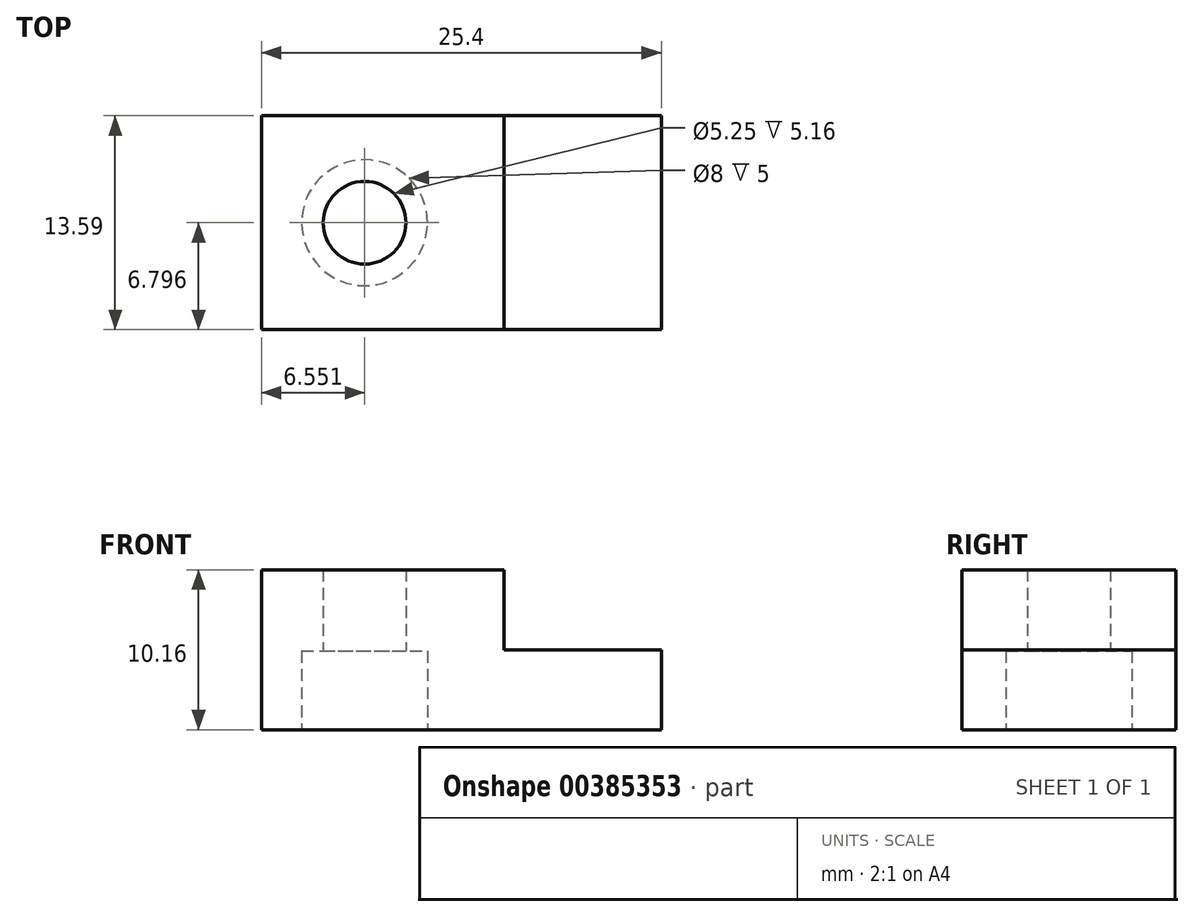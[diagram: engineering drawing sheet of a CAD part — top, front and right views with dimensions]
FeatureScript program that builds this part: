
annotation { "Feature Type Name" : "Feature", "Feature Type Description" : "" }
export const myFeature = defineFeature(function(context is Context, id is Id, definition is map)
    precondition{}
    {
        {
            var Q0;
            Q0=qCreatedBy(makeId("Top.planeOp"),FACE);
            var sketch = newSketch(context, id + "F0", { "sketchPlane" : qUnion([Q0])});
            skLineSegment(sketch, "E0.bottom", {"start": v(0, 0) * mm, "end": v(25.4, 0) * mm});
            skLineSegment(sketch, "E0.top", {"start": v(0, 13.6) * mm, "end": v(25.4, 13.6) * mm});
            skLineSegment(sketch, "E0.left", {"start": v(0, 0) * mm, "end": v(0, 13.6) * mm});
            skLineSegment(sketch, "E0.right", {"start": v(25.4, 0) * mm, "end": v(25.4, 13.6) * mm});
            skPoint(sketch, "E1", {"position": v(6.55, 6.8) * mm});
            skPoint(sketch, "E1.positionSnap0", {"position": v(0, 6.8) * mm});
            skSolve(sketch);
        }
        {
            var Q0;
            Q0=makeQuery(id+"F0.imprint","IMPRINT",FACE,{"disambiguationData":[TD([[makeQuery(id+"F0.imprint","IMPRINT",EDGE,{"derivedFrom":sQuery(id+"F0.wireOp",EDGE,"E0.bottom")}),1.0]])]});
            extrude(context, id + "F1", {"entities" : qUnion([Q0]), "depth" : 10.16 * mm});
        }
        {
            var Q0;
            Q0=sQuery(id+"F0.wireOp",VERTEX,"E1");
            var Q1;
            Q1=makeQuery(id+"F1.opExtrude","SWEPT_BODY",BODY,{"disambiguationData":[OSD([sQuery(id+"F0.wireOp",EDGE,"E0.bottom"),sQuery(id+"F0.wireOp",EDGE,"E0.top"),sQuery(id+"F0.wireOp",EDGE,"E0.left"),sQuery(id+"F0.wireOp",EDGE,"E0.right")])]});
            hole(context, id + "F2", {"style" : HoleStyle.C_BORE, "endStyle" : HoleEndStyle.THROUGH, "oppositeDirection" : true, "holeDiameter" : 5.25 * mm, "cBoreDiameter" : 8 * mm, "cBoreDepth" : 5 * mm, "isTappedThrough" : true, "tappedDepth" : 12.7 * mm, "tapClearance" : 3, "startFromSketch" : true, "locations" : qUnion([Q0]), "scope" : qUnion([Q1])});
        }
        {
            var Q0;
            Q0=makeQuery(id+"F1.opExtrude","SWEPT_FACE",FACE,{"disambiguationData":[OSD([sQuery(id+"F0.wireOp",EDGE,"E0.top")])]});
            var sketch = newSketch(context, id + "F3", { "sketchPlane" : qUnion([Q0])});
            skLineSegment(sketch, "E2.bottom", {"start": v(-25.4, 10.16) * mm, "end": v(-15.4, 10.16) * mm});
            skLineSegment(sketch, "E2.top", {"start": v(-25.4, 5.08) * mm, "end": v(-15.4, 5.08) * mm});
            skLineSegment(sketch, "E2.left", {"start": v(-25.4, 10.16) * mm, "end": v(-25.4, 5.08) * mm});
            skLineSegment(sketch, "E2.right", {"start": v(-15.4, 10.16) * mm, "end": v(-15.4, 5.08) * mm});
            skSolve(sketch);
        }
        {
            var Q0;
            Q0=makeQuery(id+"F3.imprint","IMPRINT",FACE,{"disambiguationData":[TD([[makeQuery(id+"F3.imprint","IMPRINT",EDGE,{"derivedFrom":sQuery(id+"F3.wireOp",EDGE,"E2.bottom")}),1.0]])]});
            extrude(context, id + "F4", {"entities" : qUnion([Q0]), "operationType" : NewBodyOperationType.REMOVE, "oppositeDirection" : true, "depth" : 25.4 * mm});
        }
    });
